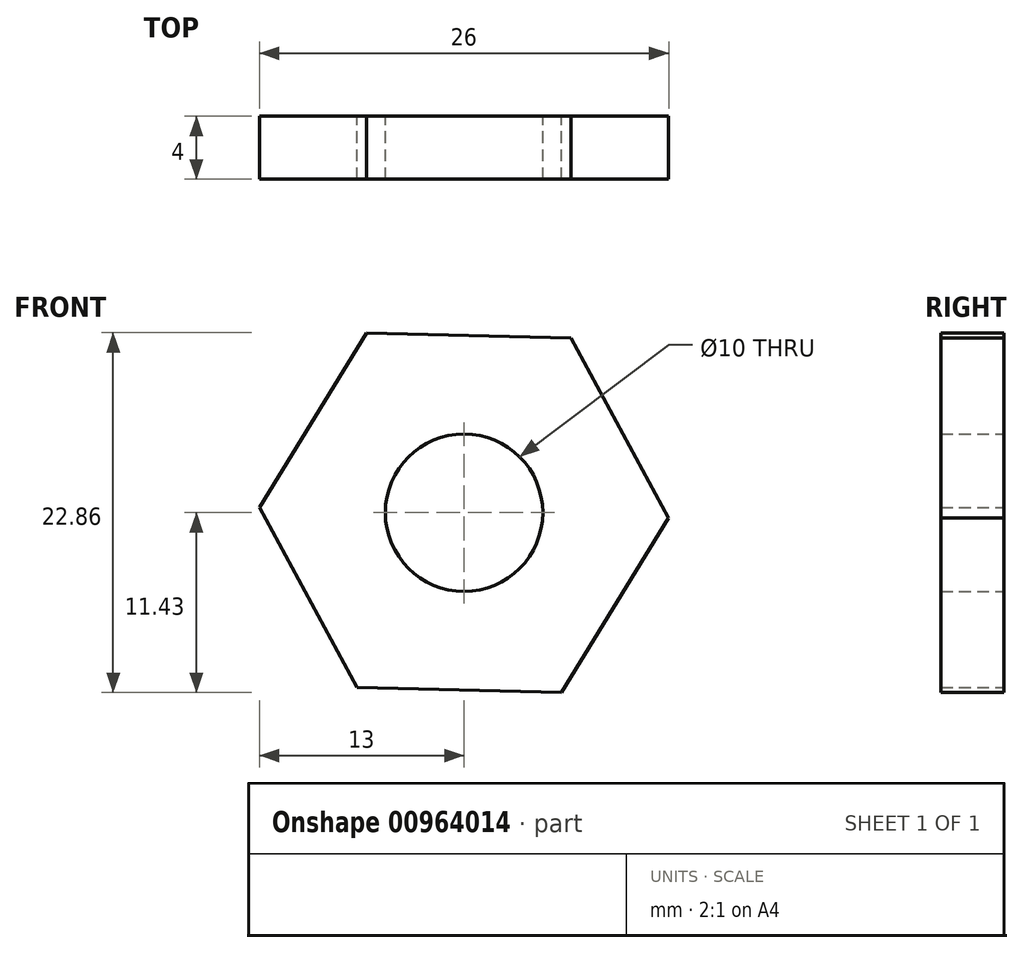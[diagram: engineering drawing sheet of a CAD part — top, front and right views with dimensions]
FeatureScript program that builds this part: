
annotation { "Feature Type Name" : "Feature", "Feature Type Description" : "" }
export const myFeature = defineFeature(function(context is Context, id is Id, definition is map)
    precondition{}
    {
        {
            var Q0;
            Q0=qCreatedBy(makeId("Front.planeOp"),FACE);
            var sketch = newSketch(context, id + "F0", { "sketchPlane" : qUnion([Q0])});
            skCircle(sketch, "E0.cCircle", {"center": v(0, 0) * mm, "radius": 11.26 * mm, "construction": true});
            skLineSegment(sketch, "E0.0", {"start": v(13, -0.34) * mm, "end": v(6.2, -11.43) * mm});
            skLineSegment(sketch, "E0.1", {"start": v(6.2, -11.43) * mm, "end": v(-6.8, -11.08) * mm});
            skLineSegment(sketch, "E0.2", {"start": v(-6.8, -11.08) * mm, "end": v(-13, 0.34) * mm});
            skLineSegment(sketch, "E0.3", {"start": v(-13, 0.34) * mm, "end": v(-6.2, 11.43) * mm});
            skLineSegment(sketch, "E0.4", {"start": v(-6.2, 11.43) * mm, "end": v(6.8, 11.08) * mm});
            skLineSegment(sketch, "E0.5", {"start": v(6.8, 11.08) * mm, "end": v(13, -0.34) * mm});
            skPoint(sketch, "E0.0.midPoint", {"position": v(9.6, -5.88) * mm});
            skCircle(sketch, "E1", {"center": v(0, 0) * mm, "radius": 5 * mm});
            skSolve(sketch);
        }
        {
            var Q0;
            Q0=makeQuery(id+"F0.imprint","IMPRINT",FACE,{"disambiguationData":[TD([[makeQuery(id+"F0.imprint","IMPRINT",EDGE,{"derivedFrom":sQuery(id+"F0.wireOp",EDGE,"E0.0")}),-1.0]])]});
            extrude(context, id + "F1", {"entities" : qUnion([Q0]), "depth" : 4 * mm, "offsetDistance" : 25 * mm});
        }
    });
